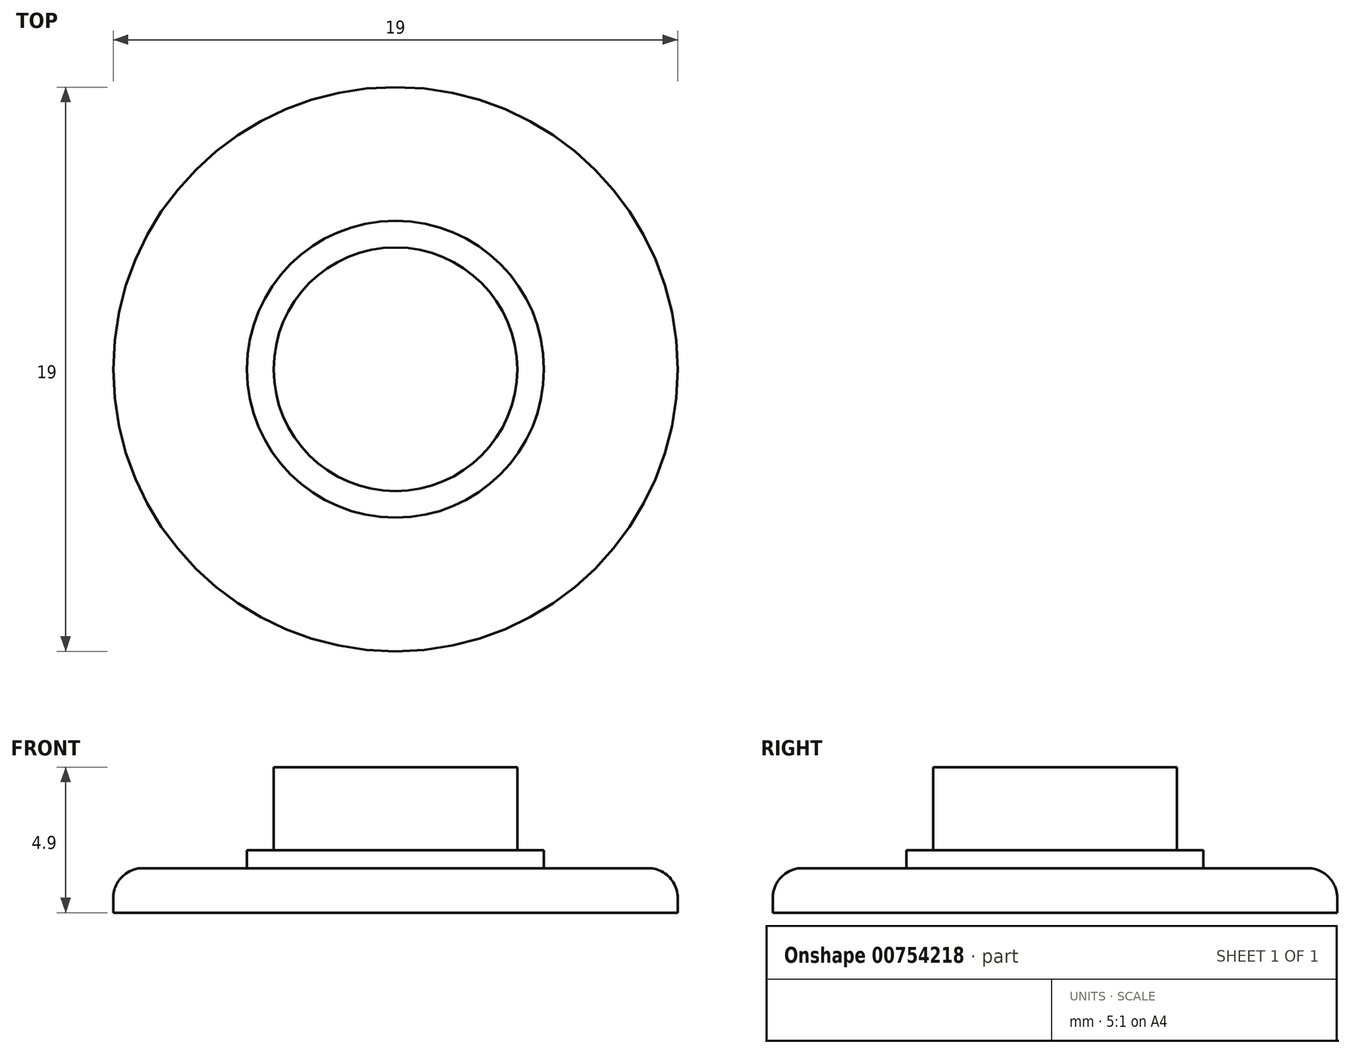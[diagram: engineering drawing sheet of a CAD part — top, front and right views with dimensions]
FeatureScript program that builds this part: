
annotation { "Feature Type Name" : "Feature", "Feature Type Description" : "" }
export const myFeature = defineFeature(function(context is Context, id is Id, definition is map)
    precondition{}
    {
        {
            var Q0;
            Q0=qCreatedBy(makeId("Top.planeOp"),FACE);
            var sketch = newSketch(context, id + "F0", { "sketchPlane" : qUnion([Q0])});
            skCircle(sketch, "E0", {"center": v(0, 0) * mm, "radius": 9.5 * mm});
            skCircle(sketch, "E1", {"center": v(0, 0) * mm, "radius": 4.1 * mm});
            skCircle(sketch, "E2", {"center": v(0, 0) * mm, "radius": 5 * mm});
            skSolve(sketch);
        }
        {
            var Q0;
            Q0=makeQuery(id+"F0.imprint","IMPRINT",FACE,{"disambiguationData":[TD([[makeQuery(id+"F0.imprint","IMPRINT",EDGE,{"derivedFrom":sQuery(id+"F0.wireOp",EDGE,"E1")}),1.0]])]});
            var Q1;
            Q1=makeQuery(id+"F0.imprint","IMPRINT",FACE,{"disambiguationData":[TD([[makeQuery(id+"F0.imprint","IMPRINT",EDGE,{"derivedFrom":sQuery(id+"F0.wireOp",EDGE,"E1")}),-1.0]])]});
            var Q2;
            Q2=makeQuery(id+"F0.imprint","IMPRINT",FACE,{"disambiguationData":[TD([[makeQuery(id+"F0.imprint","IMPRINT",EDGE,{"derivedFrom":sQuery(id+"F0.wireOp",EDGE,"E0")}),1.0]])]});
            extrude(context, id + "F1", {"entities" : qUnion([Q0, Q1, Q2]), "oppositeDirection" : true, "depth" : 1.5 * mm, "offsetDistance" : 25 * mm});
        }
        {
            var Q0;
            Q0=makeQuery(id+"F0.imprint","IMPRINT",FACE,{"disambiguationData":[TD([[makeQuery(id+"F0.imprint","IMPRINT",EDGE,{"derivedFrom":sQuery(id+"F0.wireOp",EDGE,"E1")}),1.0]])]});
            extrude(context, id + "F2", {"entities" : qUnion([Q0]), "operationType" : NewBodyOperationType.ADD, "depth" : 3.4 * mm, "offsetDistance" : 25 * mm});
        }
        {
            var Q0;
            Q0=makeQuery(id+"F0.imprint","IMPRINT",FACE,{"disambiguationData":[TD([[makeQuery(id+"F0.imprint","IMPRINT",EDGE,{"derivedFrom":sQuery(id+"F0.wireOp",EDGE,"E1")}),-1.0]])]});
            extrude(context, id + "F3", {"entities" : qUnion([Q0]), "operationType" : NewBodyOperationType.ADD, "depth" : 0.6 * mm, "offsetDistance" : 25 * mm});
        }
        {
            var Q0;
            Q0=makeQuery(id+"F1.opExtrude","CAP_EDGE",EDGE,{"disambiguationData":[OSD([sQuery(id+"F0.wireOp",EDGE,"E0")])],"isStart":true});
            fillet(context, id + "F4", {"entities" : qUnion([Q0]), "radius" : 1 * mm, "tangentPropagation" : true, "allowEdgeOverflow" : false});
        }
    });
